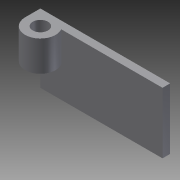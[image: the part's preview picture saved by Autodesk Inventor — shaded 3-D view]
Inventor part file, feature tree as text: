
AUTODESK INVENTOR PART (.ipt)
format: ipt  version: 2011 (Build 150239000, 239)  size: 126,976 bytes
history: native  units: in
note: dims shown in document units (in); Inventor stores cm internally (conversion verified against a paired STEP export)
features: extrude x7, sketch x7
ambient origin geometry x8: Origin, YZ Plane, XZ Plane, XY Plane, X Axis, Y Axis, Z Axis, Center Point
bodies: Solid1 (feature_tree)
feature tree (14):
  extrude  "Extrusion1"  Depth=1.0in
  extrude  "Extrusion2"  Depth=0.125in
  extrude  "Extrusion3"  Depth=0.5in TaperAngle=0.0deg
  extrude  "Extrusion4"  Depth=0.5in TaperAngle=0.0deg
  extrude  "Extrusion5"  Depth=0.125in
  extrude  "Extrusion6"  Depth=0.5in TaperAngle=0.0deg
  extrude  "Extrusion7"  [1 undecoded]
  sketch  "Sketch1"  dims[d0=2.0in d1=1.0in]
  sketch  "Sketch2"  dims[d2=0.125in d3=0.0in d4=0.125in]
  sketch  "Sketch3"  dims[d5=0.125in d6=0.5in d7=0.0in]
  sketch  "Sketch4"  dims[d8=0.5in d9=0.0in d10=0.5in d11=0.0in]
  sketch  "Sketch5"  dims[d12=1.0in d13=0.0in d14=0.125in]
  sketch  "Sketch6"  dims[d15=0.125in d16=0.5in d17=0.0in]
  sketch  "Sketch7"  dims[d18=0.5in d19=0.0in]
note: 1 required parameter value undecoded (feature->parameter linkage not recoverable at this tier; creation-order binding heuristic only, values carry confidence <= 0.55)
